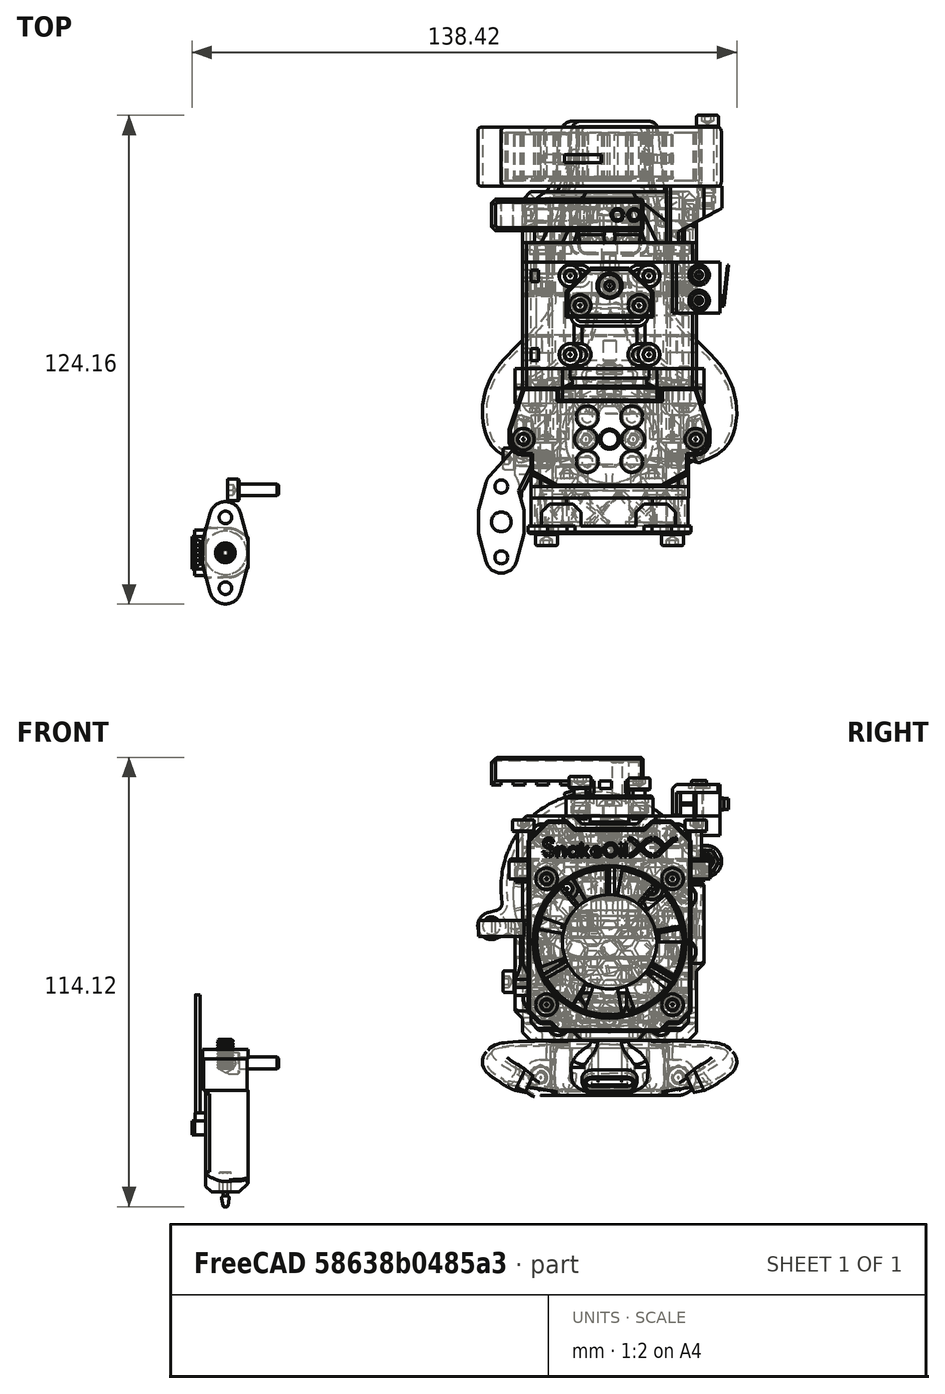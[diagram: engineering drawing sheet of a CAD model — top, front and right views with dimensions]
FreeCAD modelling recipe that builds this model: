
FCSTD DOCUMENT  (FreeCAD 0.19R24291 (Git))
Label: toolhead-carrier-sherpa-1515-assembly
License: Other
LicenseURL: GPL3
objects: Part::FeaturePython×61, Part::Feature×55, App::Part×3, PartDesign::CoordinateSystem×1
note: 117 computed .brp shape members not serialized (recipe doc carries the construction recipe); baked Part::Feature solids carry a one-line shape summary decoded from their .brp

FEATURE [Part::FeaturePython] Screw1376  label="M2.5x12-Screw"  # Fasteners workbench fastener (typed FeaturePython)
  Placement = pos=(-6,-31.5,29.2) rot=(0,0,1;0rad)
  diameter = 3
  invert = false
  length = 10
  lengthCustom = 12
  matchOuter = true
  offset = 10
  thread = false
  type = 33
FEATURE [Part::FeaturePython] Screw1377  label="M2.5x12-Screw001"  # Fasteners workbench fastener (typed FeaturePython)
  Placement = pos=(6,-31.5,29.2) rot=(0,0,1;0rad)
  diameter = 3
  invert = false
  length = 10
  lengthCustom = 12
  matchOuter = true
  offset = 10
  thread = false
  type = 33
FEATURE [Part::Feature] Part__Feature023  label="adxl345 v026"
  shape: bbox 0.1911 x 0.3 x 0.1 mm, 6 faces (baked)
FEATURE [Part::Feature] Part__Feature016  label="adxl345 v019"
  shape: bbox 0.5 x 0.5 x 0.1 mm, 6 faces (baked)
FEATURE [Part::Feature] Part__Feature017  label="adxl345 v020"
  shape: bbox 0.5 x 0.5 x 0.1 mm, 6 faces (baked)
FEATURE [Part::Feature] Part__Feature112001127  label="adxl345 v017"
  shape: bbox 0.5 x 0.5 x 0.1 mm, 6 faces (baked)
FEATURE [Part::Feature] Part__Feature112001128  label="adxl345 v004"
  shape: bbox 20 x 15 x 1.27 mm, 8 faces (baked)
FEATURE [Part::Feature] Part__Feature013  label="adxl345 v016"
  shape: bbox 0.1939 x 0.3 x 0.1 mm, 6 faces (baked)
FEATURE [Part::Feature] Part__Feature112001129  label="adxl345 v3"
  shape: bbox 6 x 3 x 0.5 mm, 6 faces (baked)
FEATURE [Part::Feature] Part__Feature030  label="adxl345 v033"
  shape: bbox 0.5 x 0.5 x 0.15 mm, 6 faces (baked)
FEATURE [Part::Feature] Part__Feature112001123  label="adxl345 v012"
  shape: bbox 0.5 x 0.5 x 0.1 mm, 6 faces (baked)
FEATURE [Part::Feature] Part__Feature112001124  label="adxl345 v010"
  shape: bbox 0.5 x 0.5 x 0.1 mm, 6 faces (baked)
FEATURE [Part::Feature] Part__Feature005  label="adxl345 v008"
  shape: bbox 0.5 x 0.5 x 0.1 mm, 6 faces (baked)
FEATURE [Part::Feature] Part__Feature004  label="adxl345 v007"
  shape: bbox 0.5 x 0.5 x 0.1 mm, 6 faces (baked)
FEATURE [Part::Feature] Part__Feature112001125  label="adxl345 v006"
  shape: bbox 0.2125 x 0.3 x 0.1 mm, 6 faces (baked)
FEATURE [Part::Feature] Part__Feature112001126  label="adxl345 v005"
  shape: bbox 4 x 2 x 1 mm, 6 faces (baked)
FEATURE [Part::Feature] Part__Feature012  label="adxl345 v015"
  shape: bbox 0.2125 x 0.4 x 0.1 mm, 6 faces (baked)
FEATURE [Part::Feature] Part__Feature025  label="adxl345 v028"
  shape: bbox 0.5 x 0.5 x 0.15 mm, 6 faces (baked)
FEATURE [Part::Feature] Part__Feature026  label="adxl345 v029"
  shape: bbox 0.5 x 0.5054 x 0.15 mm, 6 faces (baked)
FEATURE [Part::Feature] Part__Feature027  label="adxl345 v030"
  shape: bbox 0.5 x 0.5 x 0.15 mm, 6 faces (baked)
FEATURE [Part::Feature] Part__Feature028  label="adxl345 v031"
  shape: bbox 0.5 x 0.5054 x 0.15 mm, 6 faces (baked)
FEATURE [Part::Feature] Part__Feature029  label="adxl345 v032"
  shape: bbox 0.5 x 0.5054 x 0.15 mm, 6 faces (baked)
FEATURE [Part::Feature] Part__Feature015  label="adxl345 v018"
  shape: bbox 0.5 x 0.5 x 0.1 mm, 6 faces (baked)
FEATURE [Part::Feature] Part__Feature112001131  label="4010-fan"
  Placement = pos=(-2.4e-14,-43.5,14) rot=(0,0,1;0rad)
  shape: bbox 40 x 10 x 40 mm, 104 faces (baked)
FEATURE [Part::FeaturePython] Screw1373  label="M3x20-Screw024"  # Fasteners workbench fastener (typed FeaturePython)
  Placement = pos=(16,-55.5,30) rot=(1,0,0;1.5708rad)
  baseObject = -> Part__Feature112001131 [Edge124]
  diameter = 4
  invert = false
  length = 10
  lengthCustom = 20
  matchOuter = true
  offset = 2
  thread = false
  type = 33
FEATURE [Part::FeaturePython] Screw1374  label="M3x25-Screw004"  # Fasteners workbench fastener (typed FeaturePython)
  Placement = pos=(-16,-55.5,-2) rot=(1,0,0;1.5708rad)
  baseObject = -> Part__Feature112001131 [Edge127]
  diameter = 4
  invert = false
  length = 10
  lengthCustom = 25
  matchOuter = true
  offset = 2
  thread = false
  type = 33
FEATURE [Part::FeaturePython] Screw1375  label="M3x25-Screw029"  # Fasteners workbench fastener (typed FeaturePython)
  Placement = pos=(16,-55.5,-2) rot=(1,0,0;1.5708rad)
  baseObject = -> Part__Feature112001131 [Edge121]
  diameter = 4
  invert = false
  length = 10
  lengthCustom = 25
  matchOuter = true
  offset = 2
  thread = false
  type = 33
FEATURE [Part::FeaturePython] Screw1372  label="M3x20-Screw023"  # Fasteners workbench fastener (typed FeaturePython)
  Placement = pos=(-16,-55.5,30) rot=(1,0,0;1.5708rad)
  baseObject = -> Part__Feature112001131 [Edge130]
  diameter = 4
  invert = false
  length = 10
  lengthCustom = 20
  matchOuter = true
  offset = 2
  thread = false
  type = 33
FEATURE [Part::Feature] Part__Feature112001141  label="adxl345 v011"
  shape: bbox 0.5 x 2 x 0.1 mm, 6 faces (baked)
FEATURE [Part::Feature] Part__Feature112001140  label="adxl345 v009"
  shape: bbox 0.5 x 0.4946 x 0.1 mm, 6 faces (baked)
FEATURE [Part::Feature] Part__Feature011  label="adxl345 v014"
  shape: bbox 0.5 x 0.5 x 0.1 mm, 6 faces (baked)
FEATURE [Part::Feature] Part__Feature010  label="adxl345 v013"
  shape: bbox 0.5 x 0.4946 x 0.1 mm, 6 faces (baked)
FEATURE [Part::Feature] Part__Feature018  label="adxl345 v021"
  shape: bbox 0.5 x 2 x 0.1 mm, 6 faces (baked)
FEATURE [Part::Feature] Part__Feature019  label="adxl345 v022"
  shape: bbox 0.5 x 0.4946 x 0.1 mm, 6 faces (baked)
FEATURE [Part::Feature] Part__Feature020  label="adxl345 v023"
  shape: bbox 0.5 x 0.5 x 0.1 mm, 6 faces (baked)
FEATURE [Part::Feature] Part__Feature021  label="adxl345 v024"
  shape: bbox 0.5005 x 0.4962 x 0.1 mm, 6 faces (baked)
FEATURE [Part::Feature] Part__Feature022  label="adxl345 v025"
  shape: bbox 0.1911 x 0.4 x 0.1 mm, 6 faces (baked)
FEATURE [Part::Feature] Part__Feature112001139  label="BL-touch v3.x002"
  Placement = pos=(-97.5942,-60.3565,-13.2887) rot=(0,0,1;1.5708rad)
  shape: bbox 16.53 x 26.01 x 53.81 mm, 111 faces (baked)
FEATURE [Part::FeaturePython] Nut057  label="M3-Nut026"  # Fasteners workbench fastener (typed FeaturePython)
  Placement = pos=(-17.05,15.5,41) rot=(-1,0,0;1.5708rad)
  diameter = 4
  invert = false
  matchOuter = true
  offset = 0
  thread = false
  type = 7
FEATURE [Part::FeaturePython] Nut004  label="M3-Nut009"  # Fasteners workbench fastener (typed FeaturePython)
  Placement = pos=(13,15.5,-7) rot=(-1,0,0;1.5708rad)
  diameter = 4
  invert = false
  matchOuter = true
  offset = 0
  thread = false
  type = 7
FEATURE [Part::FeaturePython] Nut005  label="M3-Nut030"  # Fasteners workbench fastener (typed FeaturePython)
  Placement = pos=(-13,15.5,-7) rot=(-1,0,0;1.5708rad)
  diameter = 4
  invert = false
  matchOuter = true
  offset = 0
  thread = false
  type = 7
FEATURE [Part::FeaturePython] Screw1359  label="M3x35-Screw004"  # Fasteners workbench fastener (typed FeaturePython)
  Placement = pos=(-13.0042,-16,-6.99647) rot=(1,0,0;1.5708rad)
  diameter = 4
  invert = true
  length = 10
  lengthCustom = 35
  matchOuter = true
  offset = 0
  thread = false
  type = 33
FEATURE [Part::FeaturePython] Screw1360  label="M3x35-Screw003"  # Fasteners workbench fastener (typed FeaturePython)
  Placement = pos=(12.9958,-16,-6.99647) rot=(1,0,0;1.5708rad)
  diameter = 4
  invert = true
  length = 10
  lengthCustom = 35
  matchOuter = true
  offset = 0
  thread = false
  type = 33
FEATURE [Part::FeaturePython] Screw020  label="M3x10-Screw"  # Fasteners workbench fastener (typed FeaturePython)
  Placement = pos=(-10.0042,-9.99647,39.1513) rot=(0,0,1;0rad)
  diameter = 4
  invert = false
  length = 10
  lengthCustom = 10
  matchOuter = true
  offset = 0
  thread = false
  type = 33
FEATURE [Part::FeaturePython] Screw022  label="M3x12-Screw"  # Fasteners workbench fastener (typed FeaturePython)
  Placement = pos=(-21.9,-31.5,42) rot=(0,0,1;0rad)
  diameter = 4
  invert = false
  length = 10
  lengthCustom = 12
  matchOuter = true
  offset = 7
  thread = false
  type = 33
FEATURE [Part::FeaturePython] Screw023  label="M3x12-Screw066"  # Fasteners workbench fastener (typed FeaturePython)
  Placement = pos=(21.9,-31.5,42) rot=(0,0,1;0rad)
  diameter = 4
  invert = false
  length = 10
  lengthCustom = 12
  matchOuter = true
  offset = 7
  thread = false
  type = 33
FEATURE [Part::FeaturePython] Screw027  label="M3x25-Screw"  # Fasteners workbench fastener (typed FeaturePython)
  Placement = pos=(-10.8,-38.5,27.5) rot=(1,0,0;1.5708rad)
  diameter = 4
  invert = false
  length = 10
  lengthCustom = 25
  matchOuter = true
  offset = 0
  thread = false
  type = 33
FEATURE [Part::FeaturePython] Screw1369  label="M3x25-Screw030"  # Fasteners workbench fastener (typed FeaturePython)
  Placement = pos=(10.8,-38.5,27.5) rot=(1,0,0;1.5708rad)
  diameter = 4
  invert = false
  length = 10
  lengthCustom = 25
  matchOuter = true
  offset = 0
  thread = false
  type = 33
FEATURE [Part::FeaturePython] Nut058  label="M3-Nut027"  # Fasteners workbench fastener (typed FeaturePython)
  Placement = pos=(17.05,15.5,41) rot=(-1,0,0;1.5708rad)
  diameter = 4
  invert = false
  matchOuter = true
  offset = 0
  thread = false
  type = 7
FEATURE [Part::FeaturePython] Screw1355  label="M3x40-Screw001"  # Fasteners workbench fastener (typed FeaturePython)
  Placement = pos=(-18.5,25.5,6) rot=(0,-1,0;1.5708rad)
  diameter = 4
  invert = false
  length = 10
  lengthCustom = 40
  matchOuter = true
  offset = 0
  thread = false
  type = 33
FEATURE [Part::FeaturePython] Screw1356  label="M3x40-Screw"  # Fasteners workbench fastener (typed FeaturePython)
  Placement = pos=(18.5,25.5,19) rot=(0,1,0;1.5708rad)
  diameter = 4
  invert = false
  length = 10
  lengthCustom = 40
  matchOuter = true
  offset = 0
  thread = false
  type = 33
FEATURE [Part::Feature] Part__Feature112001130  label="adxl345 v034"
  shape: bbox 2 x 1 x 0.3 mm, 6 faces (baked)
FEATURE [Part::Feature] Part__Feature024  label="adxl345 v027"
  shape: bbox 0.5005 x 0.5054 x 0.15 mm, 6 faces (baked)
FEATURE [App::Part] adxl345_v3  label="adxl345"
  Group = -> [Part__Feature112001129,Part__Feature112001128,Part__Feature112001126,Part__Feature112001125,Part__Feature004,Part__Feature005,Part__Feature112001140,Part__Feature112001124,Part__Feature112001141,Part__Feature112001123,Part__Feature010,Part__Feature011,Part__Feature012,Part__Feature013,Part__Feature112001127,Part__Feature015,Part__Feature016,Part__Feature017,Part__Feature018,Part__Feature019,+12 more]
  Origin = -> Origin004
  Placement = pos=(-10,0.5,52.5) rot=(0,0,1;0rad)
FEATURE [Part::Feature] Fusion006002011004053036004001028003005014018035002010  label="mosquito-hotend"
  Placement = pos=(0,-31.5,-28) rot=(0,0,1;0rad)
  shape: bbox 27.01 x 18.86 x 47.01 mm, 355 faces, 0 solids (baked)
FEATURE [Part::Feature] Part__Feature112001133  label="mosquito_support"
  Placement = pos=(-2.78e-14,-21.6,27.5) rot=(0,0,1;0rad)
  shape: bbox 40 x 20.25 x 12 mm, 97 faces (baked)
FEATURE [Part::FeaturePython] Screw026  label="M3x8-Screw128"  # Fasteners workbench fastener (typed FeaturePython)
  Placement = pos=(3e-15,-20.15,-6) rot=(1,0,0;1.5708rad)
  baseObject = -> Part__Feature112001133 [Edge213]
  diameter = 4
  invert = true
  length = 10
  lengthCustom = 8
  matchOuter = true
  offset = 0
  thread = false
  type = 33
FEATURE [Part::Feature] Part__Feature112001136  label="5015 fan"
  Placement = pos=(-4.23967,32.8,25.9455) rot=(0.15487,0.698575,0.698575;3.44889rad)
  shape: bbox 61.97 x 15 x 62.93 mm, 220 faces (baked)
FEATURE [Part::FeaturePython] Screw1368  label="M3x20-Screw"  # Fasteners workbench fastener (typed FeaturePython)
  Placement = pos=(24.8765,47.8,34.436) rot=(-1,0,0;1.5708rad)
  baseObject = -> Part__Feature112001136 [Edge8]
  diameter = 4
  invert = false
  length = 7
  lengthCustom = 20
  matchOuter = true
  offset = 0
  thread = false
  type = 33
FEATURE [Part::FeaturePython] Screw017  label="M3x10-Screw188"  # Fasteners workbench fastener (typed FeaturePython)
  Placement = pos=(9.99577,10.0035,39.1513) rot=(0,0,1;0rad)
  diameter = 4
  invert = true
  length = 10
  lengthCustom = 10
  matchOuter = true
  offset = 0
  thread = false
  type = 33
FEATURE [Part::FeaturePython] Screw018  label="M3x10-Screw186"  # Fasteners workbench fastener (typed FeaturePython)
  Placement = pos=(9.99577,-9.99647,39.1513) rot=(0,0,1;0rad)
  diameter = 4
  invert = true
  length = 10
  lengthCustom = 10
  matchOuter = true
  offset = 0
  thread = false
  type = 33
FEATURE [Part::FeaturePython] Screw019  label="M3x10-Screw187"  # Fasteners workbench fastener (typed FeaturePython)
  Placement = pos=(-10.0042,10.0035,39.1513) rot=(0,0,1;0rad)
  diameter = 4
  invert = false
  length = 10
  lengthCustom = 10
  matchOuter = true
  offset = 0
  thread = false
  type = 33
FEATURE [Part::Feature] Fusion036012039011002025018010027013001002002001002001029001  label="adxl-mount"
  Placement = pos=(0,-31.5,33) rot=(0,0,1;0rad)
  shape: bbox 22 x 12.5 x 6.5 mm, 26 faces (baked)
FEATURE [Part::FeaturePython] Screw  label="M3x8-Screw"  # Fasteners workbench fastener (typed FeaturePython)
  Placement = pos=(0,7.5,48.5) rot=(0,0,1;0rad)
  diameter = 1
  invert = false
  length = 1
  lengthCustom = 8
  matchOuter = true
  offset = 0
  thread = false
  type = 39
FEATURE [Part::FeaturePython] Screw1378  label="M3x6-Screw"  # Fasteners workbench fastener (typed FeaturePython)
  Placement = pos=(-7.5,2.5,53) rot=(0,0,1;0rad)
  baseObject = -> Fusion036012039011002025018010027013001002002001002001029001 [Edge2]
  diameter = 4
  invert = false
  length = 1
  lengthCustom = 6
  matchOuter = true
  offset = 2.4
  thread = false
  type = 33
FEATURE [Part::FeaturePython] Screw1379  label="M3x6-Screw105"  # Fasteners workbench fastener (typed FeaturePython)
  Placement = pos=(7.5,2.5,52.6) rot=(0,0,1;0rad)
  baseObject = -> Fusion036012039011002025018010027013001002002001002001029001 [Edge47]
  diameter = 4
  invert = false
  length = 1
  lengthCustom = 6
  matchOuter = true
  offset = 2
  thread = false
  type = 33
FEATURE [Part::FeaturePython] Screw1380  label="M3x35-Screw005"  # Fasteners workbench fastener (typed FeaturePython)
  Placement = pos=(-17.0542,-16.5,41.0035) rot=(1,0,0;1.5708rad)
  diameter = 1
  invert = true
  length = 9
  lengthCustom = 35
  matchOuter = true
  offset = 0
  thread = false
  type = 39
FEATURE [Part::FeaturePython] Screw1381  label="M3x35-Screw"  # Fasteners workbench fastener (typed FeaturePython)
  Placement = pos=(17.0458,-16.5,41.0035) rot=(1,0,0;1.5708rad)
  diameter = 1
  invert = true
  length = 9
  lengthCustom = 35
  matchOuter = true
  offset = 0
  thread = false
  type = 39
FEATURE [Part::Feature] Part__Feature112001143  label="dragon_support"
  Placement = pos=(-1.3e-14,-65.5,-44.5) rot=(1,0,0;3.14159rad)
  shape: bbox 40 x 20.25 x 9.266 mm, 50 faces (baked)
FEATURE [Part::Feature] Chamfer005021077002006007019003014001  label="face-plate"
  Placement = pos=(0,-56.5,-6) rot=(0,0,1;0rad)
  shape: bbox 41.5 x 7.5 x 53.5 mm, 789 faces (baked)
FEATURE [Part::Feature] Chamfer005021077002006007019003032007001  label="mosquito-mount-mod"
  Placement = pos=(0,-31.5,33) rot=(0,0,1;0rad)
  shape: bbox 51.01 x 27.77 x 40.81 mm, 154 faces (baked)
FEATURE [Part::Feature] Chamfer005021077002006007019003029001  label="dragon-mount-mod"
  Placement = pos=(0,-31.5,33) rot=(0,0,1;0rad)
  shape: bbox 51.01 x 26.2 x 43.01 mm, 143 faces (baked)
FEATURE [Part::FeaturePython] Screw1371  label="M3x10-Screw189"  # Fasteners workbench fastener (typed FeaturePython)
  Placement = pos=(-94.0942,-44.3565,-16.7887) rot=(0,-1,0;1.5708rad)
  diameter = 4
  invert = false
  length = 10
  lengthCustom = 10
  matchOuter = true
  offset = 0
  thread = false
  type = 33
FEATURE [App::Part] BL_Touch__1_001  label="BL-Touch <1>001"
  Group = -> [Part__Feature112001139,Screw1371]
  Origin = -> Origin206
  Placement = pos=(70,8,28.5) rot=(0,0,1;0rad)
FEATURE [Part::Feature] Chamfer008009001  label="extruder-belt-tesioner"
  Placement = pos=(6,15,10) rot=(0,1,0;3.14159rad)
  shape: bbox 20 x 14.4 x 10 mm, 116 faces (baked)
FEATURE [Part::Feature] Chamfer005021077002006007019003032007003  label="extruder-belt-tesioner001"
  Placement = pos=(-6,15,15) rot=(0,0,1;0rad)
  shape: bbox 20 x 14.4 x 10 mm, 116 faces (baked)
FEATURE [Part::Feature] Body001002001  label="top-plate-with-endstop"
  Placement = pos=(0,0,0) rot=(0,0,1;3.14159rad)
  shape: bbox 50.05 x 27 x 13 mm, 100 faces (baked)
FEATURE [Part::Feature] Fusion006002011004053036004001028003005014029  label="endstop-switch"
  Placement = pos=(28,7,46) rot=(0,0,1;1.5708rad)
  shape: bbox 12.18 x 13 x 6 mm, 43 faces (baked)
FEATURE [Part::Feature] Body001001001  label="endstop-cap"
  Placement = pos=(16,7,54) rot=(1,0,0;3.14159rad)
  shape: bbox 12 x 13 x 7.75 mm, 19 faces (baked)
FEATURE [Part::FeaturePython] Screw1382  label="M2x10-Screw001"  # Fasteners workbench fastener (typed FeaturePython)
  Placement = pos=(22.75,3.75,53) rot=(0,0,1;0rad)
  baseObject = -> Body001001001 [Edge27]
  diameter = 2
  invert = false
  length = 5
  lengthCustom = 10
  matchOuter = true
  offset = 0
  thread = false
  type = 33
FEATURE [Part::FeaturePython] Screw1383  label="M2x10-Screw"  # Fasteners workbench fastener (typed FeaturePython)
  Placement = pos=(22.75,10.25,53) rot=(0,0,1;0rad)
  baseObject = -> Body001001001 [Edge25]
  diameter = 2
  invert = false
  length = 5
  lengthCustom = 10
  matchOuter = true
  offset = 0
  thread = false
  type = 33
FEATURE [PartDesign::CoordinateSystem] LCS_toolhead_1515  label="LCS_toolhead-1515"
  AttacherType = Attacher::AttachEngine3D
FEATURE [Part::FeaturePython] HeatSet001  label="M3x4-HeatSet001"  # WARN: FeaturePython — macro-defined, semantics opaque (R4)
  Placement = pos=(-20,-36.5,11.7) rot=(0,-1,0;1.5708rad)
  baseObject = -> Chamfer005021077002006007019003029001 [Edge194]
  diameter = 2
  invert = false
  offset = 0
FEATURE [Part::FeaturePython] HeatSet002  label="M3x4-HeatSet003"  # WARN: FeaturePython — macro-defined, semantics opaque (R4)
  Placement = pos=(20,-36.5,11.7) rot=(0,1,0;1.5708rad)
  baseObject = -> Chamfer005021077002006007019003029001 [Edge128]
  diameter = 2
  invert = true
  offset = 0
FEATURE [Part::FeaturePython] HeatSet003  label="M3x4-HeatSet"  # WARN: FeaturePython — macro-defined, semantics opaque (R4)
  Placement = pos=(20,-36.5,3.7) rot=(0,1,0;1.5708rad)
  baseObject = -> Chamfer005021077002006007019003029001 [Edge127]
  diameter = 2
  invert = true
  offset = 0
FEATURE [Part::FeaturePython] HeatSet004  label="M3x4-HeatSet009"  # WARN: FeaturePython — macro-defined, semantics opaque (R4)
  Placement = pos=(1e-14,7.5,46) rot=(0,0,1;0rad)
  baseObject = -> Body001002001 [Edge282]
  diameter = 2
  invert = true
  offset = 0
FEATURE [Part::FeaturePython] HeatSet005  label="M3x4-HeatSet008"  # WARN: FeaturePython — macro-defined, semantics opaque (R4)
  Placement = pos=(-7.5,2.5,51) rot=(0,0,1;0rad)
  baseObject = -> Fusion036012039011002025018010027013001002002001002001029001 [Edge5]
  diameter = 2
  invert = false
  offset = 0
FEATURE [Part::FeaturePython] HeatSet006  label="M3x4-HeatSet007"  # WARN: FeaturePython — macro-defined, semantics opaque (R4)
  Placement = pos=(7.5,2.5,51) rot=(0,0,1;0rad)
  baseObject = -> Fusion036012039011002025018010027013001002002001002001029001 [Edge25]
  diameter = 2
  invert = false
  offset = 0
FEATURE [Part::FeaturePython] HeatSet014  label="M3x4-HeatSet010"  # WARN: FeaturePython — macro-defined, semantics opaque (R4)
  Placement = pos=(10.8,-13.5,27.705) rot=(-1,0,0;1.5708rad)
  diameter = 2
  invert = true
  offset = 0
FEATURE [Part::FeaturePython] HeatSet015  label="M3x4-HeatSet012"  # WARN: FeaturePython — macro-defined, semantics opaque (R4)
  Placement = pos=(-10.8,-13.5,27.71) rot=(-1,0,0;1.5708rad)
  diameter = 2
  invert = true
  offset = 0
FEATURE [Part::FeaturePython] HeatSet016  label="M3x4-HeatSet004"  # WARN: FeaturePython — macro-defined, semantics opaque (R4)
  Placement = pos=(10,25.5,6) rot=(0,1,0;1.5708rad)
  baseObject = -> Chamfer008009001 [Edge5]
  diameter = 2
  invert = false
  offset = 0
FEATURE [Part::FeaturePython] HeatSet017  label="M3x4-HeatSet013"  # WARN: FeaturePython — macro-defined, semantics opaque (R4)
  Placement = pos=(-10,25.5,19) rot=(0,-1,0;1.5708rad)
  baseObject = -> Chamfer005021077002006007019003032007003 [Edge5]
  diameter = 2
  invert = false
  offset = 0
FEATURE [Part::FeaturePython] HeatSet018  label="M3x4-HeatSet018"  # WARN: FeaturePython — macro-defined, semantics opaque (R4)
  Placement = pos=(21.9,-31.5,35) rot=(0,0,1;0rad)
  baseObject = -> Chamfer005021077002006007019003029001 [Edge25]
  diameter = 2
  invert = false
  offset = 0
FEATURE [Part::FeaturePython] HeatSet019  label="M3x4-HeatSet017"  # WARN: FeaturePython — macro-defined, semantics opaque (R4)
  Placement = pos=(-21.9,-31.5,35) rot=(0,0,1;0rad)
  baseObject = -> Chamfer005021077002006007019003029001 [Edge1]
  diameter = 2
  invert = false
  offset = 0
FEATURE [Part::FeaturePython] Nut  label="M3-Nut"  # Fasteners workbench fastener (typed FeaturePython)
  Placement = pos=(0,-15,-5.8) rot=(-1,0,0;1.5708rad)
  diameter = 4
  invert = true
  matchOuter = true
  offset = 0
  thread = false
  type = 7
FEATURE [Part::Feature] Part__Feature006  label="extruderbottom-plate"
  Placement = pos=(0,17.6378,-29.79) rot=(1,0,0;1.5708rad)
  shape: bbox 44.1 x 27 x 22.2 mm, 66 faces (baked)
FEATURE [Part::Feature] Part__Feature003  label="duct-tri-horn"
  Placement = pos=(0,10.5978,-18) rot=(1,0,0;1.5708rad)
  shape: bbox 65.34 x 50.74 x 15.61 mm, 106 faces (baked)
FEATURE [Part::FeaturePython] Nut059  label="M3-Nut032"  # Fasteners workbench fastener (typed FeaturePython)
  Placement = pos=(-17.5,8.59783,-20.5) rot=(1,0,0;1.5708rad)
  baseObject = -> Part__Feature003 [Edge75]
  diameter = 4
  invert = false
  matchOuter = true
  offset = 0
  thread = false
  type = 7
FEATURE [Part::FeaturePython] Nut060  label="M3-Nut033"  # Fasteners workbench fastener (typed FeaturePython)
  Placement = pos=(17.5,8.59783,-20.5) rot=(1,0,0;1.5708rad)
  baseObject = -> Part__Feature003 [Edge202]
  diameter = 4
  invert = true
  matchOuter = true
  offset = 0
  thread = false
  type = 7
FEATURE [Part::FeaturePython] Screw1384  label="M3x12-Screw075"  # Fasteners workbench fastener (typed FeaturePython)
  Placement = pos=(17.5,18.5,-20.5) rot=(-1,0,0;1.5708rad)
  diameter = 4
  invert = false
  length = 4
  lengthCustom = 12
  matchOuter = true
  offset = 0
  thread = false
  type = 34
FEATURE [Part::FeaturePython] Screw1385  label="M3x12-Screw074"  # Fasteners workbench fastener (typed FeaturePython)
  Placement = pos=(-17.5,18.5,-20.5) rot=(-1,0,0;1.5708rad)
  diameter = 4
  invert = true
  length = 4
  lengthCustom = 12
  matchOuter = true
  offset = 0
  thread = false
  type = 34
FEATURE [Part::Feature] Chamfer001002006002  label="extruder-cable-support"
  Placement = pos=(0,29.5,32) rot=(1,0,0;1.5708rad)
  shape: bbox 38.86 x 11.83 x 29.43 mm, 90 faces (baked)
FEATURE [Part::FeaturePython] HeatSet024  label="M3-HeatSet"  # WARN: FeaturePython — macro-defined, semantics opaque (R4)
  Placement = pos=(1.1e-14,13.5,42) rot=(-1,0,0;1.5708rad)
  diameter = 2
  invert = false
  offset = 0
FEATURE [Part::FeaturePython] Screw1386  label="M3x12-Screw076"  # Fasteners workbench fastener (typed FeaturePython)
  Placement = pos=(0,25.5,42) rot=(-1,0,0;1.5708rad)
  baseObject = -> Chamfer001002006002 [Edge216]
  diameter = 4
  invert = true
  length = 4
  lengthCustom = 12
  matchOuter = true
  offset = 0
  thread = false
  type = 34
FEATURE [Part::Feature] Chamfer005021077002006007019003032018001001  label="extruder-back-plate"
  Placement = pos=(1e-15,10,10) rot=(0,0.707107,0.707107;3.14159rad)
  shape: bbox 51.76 x 37.05 x 72.2 mm, 533 faces (baked)
FEATURE [Part::FeaturePython] HeatSet  label="M3x4-HeatSet019"  # WARN: FeaturePython — macro-defined, semantics opaque (R4)
  Placement = pos=(24.5,32.75,34.5) rot=(-1,0,0;1.5708rad)
  baseObject = -> Chamfer005021077002006007019003032018001001 [Edge361]
  diameter = 2
  invert = false
  offset = 0
FEATURE [Part::Feature] Part__Feature  label="bltouch-mount"
  Placement = pos=(0.5,-31.5,15.4) rot=(0,0,1;0rad)
  shape: bbox 13.25 x 33 x 19 mm, 31 faces (baked)
FEATURE [Part::FeaturePython] Screw1387  label="M3x10-Screw190"  # Fasteners workbench fastener (typed FeaturePython)
  Placement = pos=(-24,-36.5,3.9) rot=(0,-1,0;1.5708rad)
  baseObject = -> Part__Feature [Edge2]
  diameter = 4
  invert = false
  length = 3
  lengthCustom = 10
  matchOuter = true
  offset = 0
  thread = false
  type = 34
FEATURE [Part::Feature] Chamfer008011001001001001  label="belt-clamp-r004"
  Placement = pos=(0,-13,10) rot=(1,0,0;1.5708rad)
  shape: bbox 10.5 x 4.5 x 20 mm, 69 faces (baked)
FEATURE [Part::Feature] Chamfer008011001002001002002003001002001  label="front-plate-base-1517"
  Placement = pos=(0,-13,10) rot=(1,0,0;1.5708rad)
  shape: bbox 48 x 8 x 57 mm, 200 faces (baked)
FEATURE [Part::Feature] Chamfer005021077002006007019003032018001002  label="belt-clamp-r005"
  Placement = pos=(2.1e-15,-13,15) rot=(0,-0.707107,0.707107;3.14159rad)
  shape: bbox 10.5 x 4.5 x 20 mm, 69 faces (baked)
FEATURE [Part::FeaturePython] Washer  label="M3-Washer"  # Fasteners workbench fastener (typed FeaturePython)
  Placement = pos=(-19,-22.5,13.5) rot=(1,0,0;1.5708rad)
  baseObject = -> Chamfer005021077002006007019003032018001002 [Edge85]
  diameter = 4
  invert = false
  matchOuter = true
  offset = 0
  type = 5
FEATURE [Part::FeaturePython] Washer001  label="M3-Washer001"  # Fasteners workbench fastener (typed FeaturePython)
  Placement = pos=(-19,-22.5,-0.5) rot=(1,0,0;1.5708rad)
  baseObject = -> Chamfer005021077002006007019003032018001002 [Edge84]
  diameter = 4
  invert = false
  matchOuter = true
  offset = 0
  type = 5
FEATURE [Part::FeaturePython] Washer002  label="M3-Washer002"  # Fasteners workbench fastener (typed FeaturePython)
  Placement = pos=(19,-22.5,25.5) rot=(1,0,0;1.5708rad)
  baseObject = -> Chamfer008011001001001001 [Edge84]
  diameter = 4
  invert = false
  matchOuter = true
  offset = 0
  type = 5
FEATURE [Part::FeaturePython] Washer003  label="M3-Washer003"  # Fasteners workbench fastener (typed FeaturePython)
  Placement = pos=(19,-22.5,11.5) rot=(1,0,0;1.5708rad)
  baseObject = -> Chamfer008011001001001001 [Edge85]
  diameter = 4
  invert = false
  matchOuter = true
  offset = 0
  type = 5
FEATURE [Part::FeaturePython] Screw1388  label="M3x10-Screw191"  # Fasteners workbench fastener (typed FeaturePython)
  Placement = pos=(19,-23.05,25.5) rot=(1,0,0;1.5708rad)
  baseObject = -> Washer002 [Edge1]
  diameter = 1
  invert = false
  length = 2
  lengthCustom = 10
  matchOuter = true
  offset = 0
  thread = false
  type = 40
FEATURE [Part::FeaturePython] Screw1389  label="M3x10-Screw192"  # Fasteners workbench fastener (typed FeaturePython)
  Placement = pos=(19,-23.05,11.5) rot=(1,0,0;1.5708rad)
  baseObject = -> Washer003 [Edge1]
  diameter = 1
  invert = false
  length = 2
  lengthCustom = 10
  matchOuter = true
  offset = 0
  thread = false
  type = 40
FEATURE [Part::FeaturePython] Screw1390  label="M3x10-Screw193"  # Fasteners workbench fastener (typed FeaturePython)
  Placement = pos=(-19,-23.05,13.5) rot=(1,0,0;1.5708rad)
  baseObject = -> Washer [Edge1]
  diameter = 1
  invert = false
  length = 2
  lengthCustom = 10
  matchOuter = true
  offset = 0
  thread = false
  type = 40
FEATURE [Part::FeaturePython] Screw1391  label="M3x10-Screw194"  # Fasteners workbench fastener (typed FeaturePython)
  Placement = pos=(-19,-23.05,-0.5) rot=(1,0,0;1.5708rad)
  baseObject = -> Washer001 [Edge1]
  diameter = 1
  invert = false
  length = 2
  lengthCustom = 10
  matchOuter = true
  offset = 0
  thread = false
  type = 40
FEATURE [App::Part] Part197  label="toolhead-carrier-sherpa-1515"
  Group = -> [Fusion006002011004053036004001028003005014018035002010,Part__Feature112001133,Part__Feature112001136,Part__Feature112001131,BL_Touch__1_001,Nut058,Nut005,Nut004,Screw1355,Screw1356,Nut057,Screw1360,Screw1359,Screw1368,Screw022,Screw018,Screw020,Screw023,Screw019,Screw017,Screw026,Screw1376,Screw1377,Screw1369,Screw027,Screw1373,Screw1375,Screw1374,Screw1372,adxl345_v3,+55 more]
  Origin = -> Origin205
  Placement = pos=(0,31.5,-33) rot=(0,0,1;0rad)
